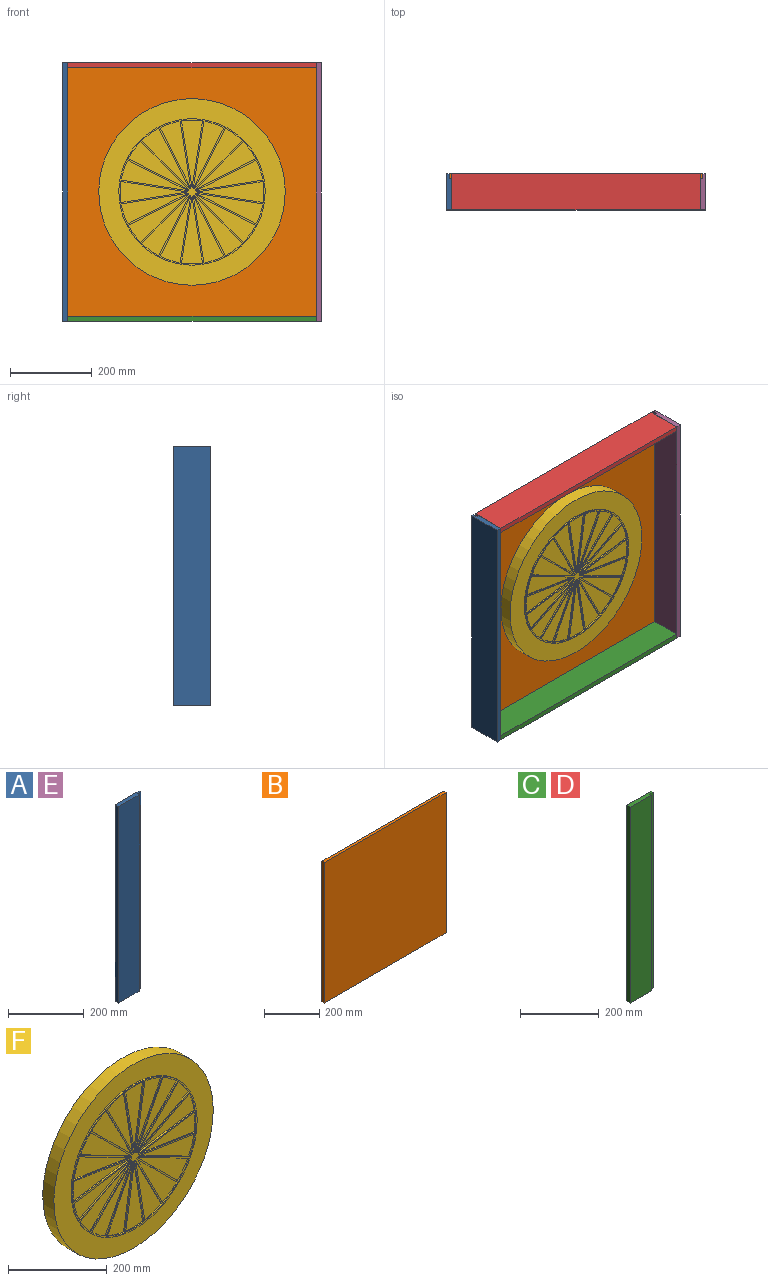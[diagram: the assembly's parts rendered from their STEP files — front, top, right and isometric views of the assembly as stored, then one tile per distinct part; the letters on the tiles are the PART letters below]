
ASSEMBLY  parts=6 mates=13
PART A: 8 faces, bbox 88.9x12.7x635 mm
  f0: plane 635x6.35mm, normal (1,0,0), area 4032.3mm2, adj f1,f3,f4,f7
  f1: plane 88.9x12.7mm, normal (0,0,1), area 1048.4mm2, adj f0,f2,f4,f5,f6,f7
  f2: plane 635x12.7mm, normal (-1,0,0), area 8064.5mm2, adj f1,f3,f4,f5
  f3: plane 88.9x12.7mm, normal (0,0,-1), area 1048.4mm2, adj f0,f2,f4,f5,f6,f7
  f4: plane 635x76.2mm, normal (0,-1,0), area 48387mm2, adj f0,f1,f2,f3
  f5: plane 635x88.9mm, normal (0,1,0), area 56451.5mm2, adj f1,f2,f3,f6
  f6: plane 635x6.35mm, normal (1,0,0), area 4032.3mm2, adj f1,f3,f5,f7
  f7: plane 635x12.7mm, normal (0,-1,0), area 8064.5mm2, adj f0,f1,f3,f6
PART B: 6 faces, bbox 622.3x12.7x622.3 mm
  f0: plane 622.3x12.7mm, normal (0,0,-1), area 7903.2mm2, adj f1,f3,f4,f5
  f1: plane 622.3x12.7mm, normal (1,0,0), area 7903.2mm2, adj f0,f2,f4,f5
  f2: plane 622.3x12.7mm, normal (0,0,1), area 7903.2mm2, adj f1,f3,f4,f5
  f3: plane 622.3x12.7mm, normal (-1,0,0), area 7903.2mm2, adj f0,f2,f4,f5
  f4: plane 622.3x622.3mm, normal (0,-1,0), area 387257.3mm2, adj f0,f1,f2,f3
  f5: plane 622.3x622.3mm, normal (0,1,0), area 387257.3mm2, adj f0,f1,f2,f3
PART C: 8 faces, bbox 88.9x12.7x609.6 mm
  f0: plane 609.6x6.35mm, normal (1,0,0), area 3871mm2, adj f1,f3,f4,f7
  f1: plane 88.9x12.7mm, normal (0,0,1), area 1048.4mm2, adj f0,f2,f4,f5,f6,f7
  f2: plane 609.6x12.7mm, normal (-1,0,0), area 7741.9mm2, adj f1,f3,f4,f5
  f3: plane 88.9x12.7mm, normal (0,0,-1), area 1048.4mm2, adj f0,f2,f4,f5,f6,f7
  f4: plane 609.6x76.2mm, normal (0,-1,0), area 46451.5mm2, adj f0,f1,f2,f3
  f5: plane 609.6x88.9mm, normal (0,1,0), area 54193.4mm2, adj f1,f2,f3,f6
  f6: plane 609.6x6.35mm, normal (1,0,0), area 3871mm2, adj f1,f3,f5,f7
  f7: plane 609.6x12.7mm, normal (0,-1,0), area 7741.9mm2, adj f0,f1,f3,f6
PART D: same geometry as C
PART E: same geometry as A
PART F: 85 faces, bbox 457.2x34.9x457.2 mm
  f0: cylinder r=228.6mm len=457.2mm, axis (0,1,0), area 45603.7mm2, adj f1,f3
  f1: plane 457.2x457.2mm, normal (0,1,0), area 164173.2mm2, adj f0
  f2: cylinder r=179.39mm len=358.78mm, axis (0,-1,0), area 3578.6mm2, adj f3,f4
  f3: plane 457.2x457.2mm, normal (0,-1,0), area 63077.2mm2, adj f0,f2
  f4: plane 358.78x358.78mm, normal (0,-1,0), area 14418.1mm2, adj f2,f5,f6,f7,f9,f10,f11,f13
  f5: cylinder r=176.21mm len=49.45mm, axis (0,-1,0), area 165.7mm2, adj f4,f6,f7,f8
  f6: plane 164.14x26mm, normal (0.99,0,-0.16), area 527.6mm2, adj f4,f5,f7,f8
  f7: plane 148.07x75.45mm, normal (-0.89,0,0.45), area 527.6mm2, adj f4,f5,f6,f8
  f8: plane 164.14x75.45mm, normal (0,-1,0), area 4333.9mm2, adj f5,f6,f7
  f9: cylinder r=176.21mm len=42.06mm, axis (0,-1,0), area 165.7mm2, adj f4,f10,f11,f12
  f10: plane 148.07x75.45mm, normal (0.89,0,-0.45), area 527.6mm2, adj f4,f9,f11,f12
  f11: plane 117.51x117.51mm, normal (-0.71,0,0.71), area 527.6mm2, adj f4,f9,f10,f12
  f12: plane 148.07x117.51mm, normal (0,-1,0), area 4333.9mm2, adj f9,f10,f11
  f13: plane 148.07x75.45mm, normal (0.89,0,0.45), area 527.6mm2, adj f4,f14,f15,f16
  f14: plane 164.14x26mm, normal (-0.99,0,-0.16), area 527.6mm2, adj f4,f13,f15,f16
  f15: cylinder r=176.21mm len=49.45mm, axis (0,-1,0), area 165.7mm2, adj f4,f13,f14,f16
  f16: plane 164.14x75.45mm, normal (0,-1,0), area 4333.9mm2, adj f13,f14,f15
  f17: cylinder r=176.21mm len=51.99mm, axis (0,-1,0), area 165.7mm2, adj f4,f18,f19,f20
  f18: plane 164.14x26mm, normal (0.99,0,0.16), area 527.6mm2, adj f4,f17,f19,f20
  f19: plane 164.14x26mm, normal (-0.99,0,0.16), area 527.6mm2, adj f4,f17,f18,f20
  f20: plane 166.06x51.99mm, normal (0,-1,0), area 4333.9mm2, adj f17,f18,f19
  f21: plane 117.51x117.51mm, normal (-0.71,0,0.71), area 527.6mm2, adj f4,f22,f23,f24
  f22: plane 148.07x75.45mm, normal (0.45,0,-0.89), area 527.6mm2, adj f4,f21,f23,f24
  f23: cylinder r=176.21mm len=42.06mm, axis (0,-1,0), area 165.7mm2, adj f4,f21,f22,f24
  f24: plane 148.07x117.51mm, normal (0,-1,0), area 4333.9mm2, adj f21,f22,f23
  f25: plane 148.07x75.45mm, normal (-0.45,0,0.89), area 527.6mm2, adj f4,f26,f27,f28
  f26: plane 164.14x26mm, normal (0.16,0,-0.99), area 527.6mm2, adj f4,f25,f27,f28
  f27: cylinder r=176.21mm len=49.45mm, axis (0,-1,0), area 165.7mm2, adj f4,f25,f26,f28
  f28: plane 164.14x75.45mm, normal (0,-1,0), area 4333.9mm2, adj f25,f26,f27
  f29: plane 164.14x26mm, normal (-0.99,0,0.16), area 527.6mm2, adj f4,f30,f31,f32
  f30: plane 148.07x75.45mm, normal (0.89,0,-0.45), area 527.6mm2, adj f4,f29,f31,f32
  f31: cylinder r=176.21mm len=49.45mm, axis (0,-1,0), area 165.7mm2, adj f4,f29,f30,f32
  f32: plane 164.14x75.45mm, normal (0,-1,0), area 4333.9mm2, adj f29,f30,f31
  f33: plane 148.07x75.45mm, normal (-0.89,0,0.45), area 527.6mm2, adj f4,f34,f35,f36
  f34: plane 117.51x117.51mm, normal (0.71,0,-0.71), area 527.6mm2, adj f4,f33,f35,f36
  f35: cylinder r=176.21mm len=42.06mm, axis (0,-1,0), area 165.7mm2, adj f4,f33,f34,f36
  f36: plane 148.07x117.51mm, normal (0,-1,0), area 4333.9mm2, adj f33,f34,f35
  f37: plane 148.07x75.45mm, normal (0.45,0,0.89), area 527.6mm2, adj f4,f38,f39,f40
  f38: plane 117.51x117.51mm, normal (-0.71,0,-0.71), area 527.6mm2, adj f4,f37,f39,f40
  f39: cylinder r=176.21mm len=42.06mm, axis (0,-1,0), area 165.7mm2, adj f4,f37,f38,f40
  f40: plane 148.07x117.51mm, normal (0,-1,0), area 4333.9mm2, adj f37,f38,f39
  f41: plane 117.51x117.51mm, normal (0.71,0,0.71), area 527.6mm2, adj f4,f42,f43,f44
  f42: plane 148.07x75.45mm, normal (-0.89,0,-0.45), area 527.6mm2, adj f4,f41,f43,f44
  f43: cylinder r=176.21mm len=42.06mm, axis (0,-1,0), area 165.7mm2, adj f4,f41,f42,f44
  f44: plane 148.07x117.51mm, normal (0,-1,0), area 4333.9mm2, adj f41,f42,f43
  f45: plane 164.14x26mm, normal (-0.16,0,0.99), area 527.6mm2, adj f4,f46,f47,f48
  f46: plane 164.14x26mm, normal (-0.16,0,-0.99), area 527.6mm2, adj f4,f45,f47,f48
  f47: cylinder r=176.21mm len=51.99mm, axis (0,-1,0), area 165.7mm2, adj f4,f45,f46,f48
  f48: plane 166.06x51.99mm, normal (0,-1,0), area 4333.9mm2, adj f45,f46,f47
  f49: plane 164.14x26mm, normal (0.16,0,0.99), area 527.6mm2, adj f4,f50,f51,f52
  f50: plane 148.07x75.45mm, normal (-0.45,0,-0.89), area 527.6mm2, adj f4,f49,f51,f52
  f51: cylinder r=176.21mm len=49.45mm, axis (0,-1,0), area 165.7mm2, adj f4,f49,f50,f52
  f52: plane 164.14x75.45mm, normal (0,-1,0), area 4333.9mm2, adj f49,f50,f51
  f53: cylinder r=176.21mm len=51.99mm, axis (0,-1,0), area 165.7mm2, adj f4,f54,f55,f56
  f54: plane 164.14x26mm, normal (0.16,0,-0.99), area 527.6mm2, adj f4,f53,f55,f56
  f55: plane 164.14x26mm, normal (0.16,0,0.99), area 527.6mm2, adj f4,f53,f54,f56
  f56: plane 166.06x51.99mm, normal (0,-1,0), area 4333.9mm2, adj f53,f54,f55
  f57: plane 148.07x75.45mm, normal (0.45,0,0.89), area 527.6mm2, adj f4,f58,f59,f60
  f58: cylinder r=176.21mm len=49.45mm, axis (0,-1,0), area 165.7mm2, adj f4,f57,f59,f60
  f59: plane 164.14x26mm, normal (-0.16,0,-0.99), area 527.6mm2, adj f4,f57,f58,f60
  f60: plane 164.14x75.45mm, normal (0,-1,0), area 4333.9mm2, adj f57,f58,f59
  f61: plane 148.07x75.45mm, normal (-0.45,0,0.89), area 527.6mm2, adj f4,f62,f63,f64
  f62: cylinder r=176.21mm len=42.06mm, axis (0,-1,0), area 165.7mm2, adj f4,f61,f63,f64
  f63: plane 117.51x117.51mm, normal (0.71,0,-0.71), area 527.6mm2, adj f4,f61,f62,f64
  f64: plane 148.07x117.51mm, normal (0,-1,0), area 4333.9mm2, adj f61,f62,f63
  f65: plane 164.14x26mm, normal (-0.16,0,0.99), area 527.6mm2, adj f4,f66,f67,f68
  f66: cylinder r=176.21mm len=49.45mm, axis (0,-1,0), area 165.7mm2, adj f4,f65,f67,f68
  f67: plane 148.07x75.45mm, normal (0.45,0,-0.89), area 527.6mm2, adj f4,f65,f66,f68
  f68: plane 164.14x75.45mm, normal (0,-1,0), area 4333.9mm2, adj f65,f66,f67
  f69: cylinder r=176.21mm len=49.45mm, axis (0,-1,0), area 165.7mm2, adj f4,f70,f71,f72
  f70: plane 148.07x75.45mm, normal (-0.89,0,-0.45), area 527.6mm2, adj f4,f69,f71,f72
  f71: plane 164.14x26mm, normal (0.99,0,0.16), area 527.6mm2, adj f4,f69,f70,f72
  f72: plane 164.14x75.45mm, normal (0,-1,0), area 4333.9mm2, adj f69,f70,f71
  f73: plane 164.14x26mm, normal (-0.99,0,-0.16), area 527.6mm2, adj f4,f74,f75,f76
  f74: plane 164.14x26mm, normal (0.99,0,-0.16), area 527.6mm2, adj f4,f73,f75,f76
  f75: cylinder r=176.21mm len=51.99mm, axis (0,-1,0), area 165.7mm2, adj f4,f73,f74,f76
  f76: plane 166.06x51.99mm, normal (0,-1,0), area 4333.9mm2, adj f73,f74,f75
  f77: plane 117.51x117.51mm, normal (0.71,0,0.71), area 527.6mm2, adj f4,f78,f79,f80
  f78: cylinder r=176.21mm len=42.06mm, axis (0,-1,0), area 165.7mm2, adj f4,f77,f79,f80
  f79: plane 148.07x75.45mm, normal (-0.45,0,-0.89), area 527.6mm2, adj f4,f77,f78,f80
  f80: plane 148.07x117.51mm, normal (0,-1,0), area 4333.9mm2, adj f77,f78,f79
  f81: cylinder r=176.21mm len=42.06mm, axis (0,-1,0), area 165.7mm2, adj f4,f82,f83,f84
  f82: plane 117.51x117.51mm, normal (-0.71,0,-0.71), area 527.6mm2, adj f4,f81,f83,f84
  f83: plane 148.07x75.45mm, normal (0.89,0,0.45), area 527.6mm2, adj f4,f81,f82,f84
  f84: plane 148.07x117.51mm, normal (0,-1,0), area 4333.9mm2, adj f81,f82,f83
PLACE A rot(axis=(0,0,1),90deg) t=(-316.3,-44.45,1.32)mm
PLACE B rot(axis=(0,1,0),90deg) t=(1.2,0,1.32)mm
PLACE C rot(axis=(-0.58,-0.58,0.58),120deg) t=(1.2,-44.45,-316.18)mm
PLACE D rot(axis=(0.58,0.58,0.58),120deg) t=(1.2,-44.45,318.82)mm
PLACE E rot(axis=(-0.71,-0.71,0),180deg) t=(318.7,-44.45,1.32)mm
PLACE F t=(1.2,-12.7,1.32)mm
MATE planar C.f6 <-> B.f5  axis (0,1,0) through (1.2,0,-313)mm
MATE planar E.f3 <-> D.f5  axis (0,0,1) through (312.59,-47.38,318.82)mm
MATE planar A.f7 <-> B.f0  axis (1,0,0) through (-309.95,-6.35,1.32)mm
MATE planar E.f7 <-> B.f2  axis (-1,0,0) through (312.35,-6.35,1.32)mm
MATE planar C.f3 <-> E.f4  axis (1,0,0) through (306,-47.38,-310.07)mm
MATE planar B.f1 <-> C.f7  axis (0,0,-1) through (1.2,-6.35,-309.83)mm
MATE planar F.f0 <-> B.f4  axis (0,1,0) through (1.2,-12.7,1.32)mm
MATE planar D.f6 <-> B.f5  axis (0,1,0) through (1.2,0,315.65)mm
MATE planar E.f6 <-> B.f5  axis (0,1,0) through (315.52,0,1.32)mm
MATE planar B.f4 <-> A.f0  axis (0,-1,0) through (1.2,-12.7,1.32)mm
MATE planar A.f1 <-> D.f5  axis (0,0,1) through (-310.2,-47.38,318.82)mm
MATE planar D.f3 <-> A.f4  axis (-1,0,0) through (-303.6,-47.38,312.72)mm
MATE planar D.f7 <-> B.f3  axis (0,0,-1) through (1.2,-6.35,312.47)mm
